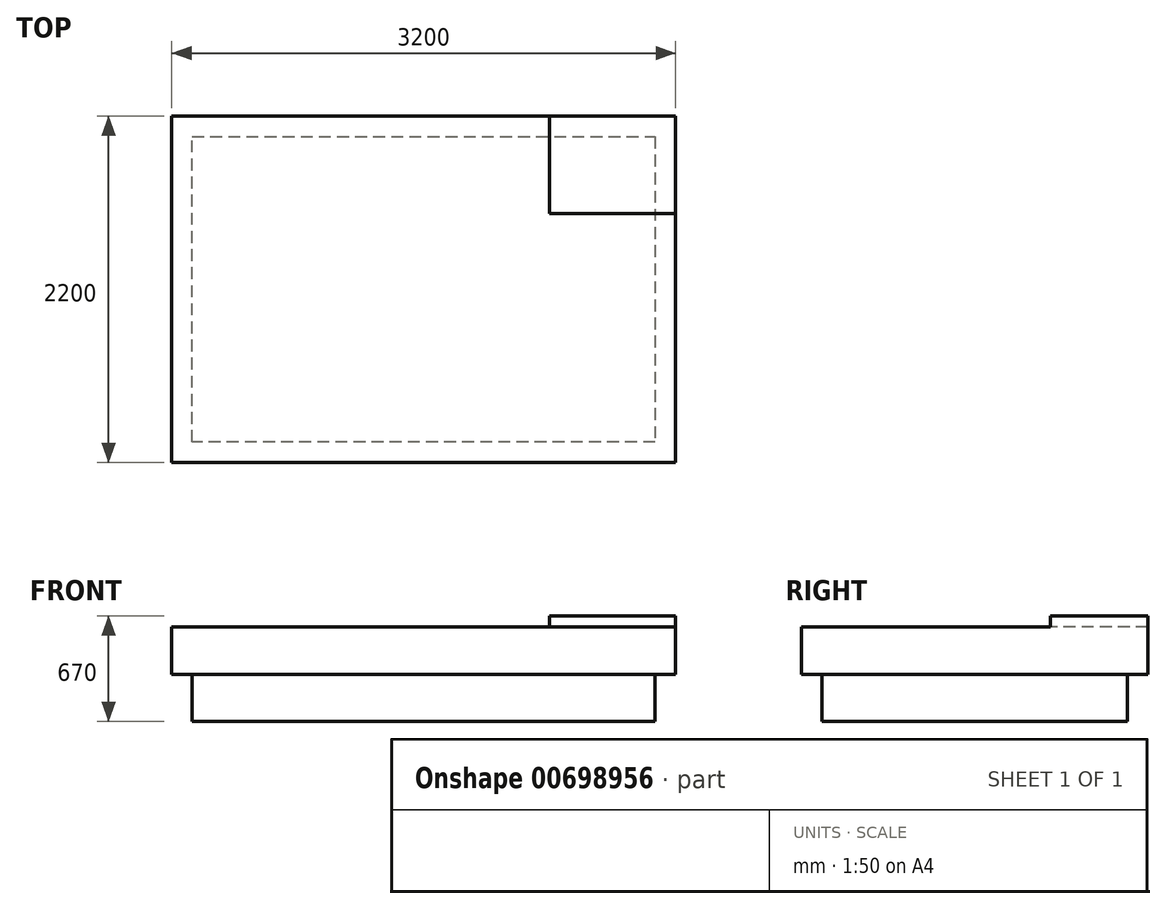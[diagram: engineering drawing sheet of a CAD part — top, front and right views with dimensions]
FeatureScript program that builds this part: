
annotation { "Feature Type Name" : "Feature", "Feature Type Description" : "" }
export const myFeature = defineFeature(function(context is Context, id is Id, definition is map)
    precondition{}
    {
        {
            var Q0;
            Q0=qCreatedBy(makeId("Top.planeOp"),FACE);
            var sketch = newSketch(context, id + "F0", { "sketchPlane" : qUnion([Q0])});
            skLineSegment(sketch, "E0.bottom", {"start": v(1600, -1100) * mm, "end": v(-1600, -1100) * mm});
            skLineSegment(sketch, "E0.top", {"start": v(1600, 1100) * mm, "end": v(-1600, 1100) * mm});
            skLineSegment(sketch, "E0.left", {"start": v(1600, -1100) * mm, "end": v(1600, 1100) * mm});
            skLineSegment(sketch, "E0.right", {"start": v(-1600, -1100) * mm, "end": v(-1600, 1100) * mm});
            skPoint(sketch, "E0.middle", {"position": v(0, 0) * mm});
            skSolve(sketch);
        }
        {
            var Q0;
            Q0 = qSketchRegion(id + "F0", true);
            extrude(context, id + "F1", {"entities" : qUnion([Q0]), "oppositeDirection" : true, "depth" : 300 * mm, "offsetDistance" : 25 * mm});
        }
        {
            var Q0;
            Q0=makeQuery(id+"F1.opExtrude","CAP_FACE",FACE,{"disambiguationData":[OSD([sQuery(id+"F0.wireOp",EDGE,"E0.bottom"),sQuery(id+"F0.wireOp",EDGE,"E0.top"),sQuery(id+"F0.wireOp",EDGE,"E0.left"),sQuery(id+"F0.wireOp",EDGE,"E0.right")])],"isStart":false});
            var sketch = newSketch(context, id + "F2", { "sketchPlane" : qUnion([Q0])});
            skLineSegment(sketch, "E1.0", {"start": v(1470, -970) * mm, "end": v(1470, 970) * mm});
            skLineSegment(sketch, "E1.1", {"start": v(-1470, -970) * mm, "end": v(1470, -970) * mm});
            skLineSegment(sketch, "E1.2", {"start": v(-1470, 970) * mm, "end": v(-1470, -970) * mm});
            skLineSegment(sketch, "E1.3", {"start": v(1470, 970) * mm, "end": v(-1470, 970) * mm});
            skSolve(sketch);
        }
        {
            var Q0;
            Q0 = qSketchRegion(id + "F2", true);
            extrude(context, id + "F3", {"entities" : qUnion([Q0]), "operationType" : NewBodyOperationType.ADD, "depth" : 300 * mm, "offsetDistance" : 25 * mm});
        }
        {
            var Q0;
            Q0=makeQuery(id+"F1.opExtrude","CAP_FACE",FACE,{"disambiguationData":[OSD([sQuery(id+"F0.wireOp",EDGE,"E0.bottom"),sQuery(id+"F0.wireOp",EDGE,"E0.top"),sQuery(id+"F0.wireOp",EDGE,"E0.left"),sQuery(id+"F0.wireOp",EDGE,"E0.right")])],"isStart":true});
            var sketch = newSketch(context, id + "F4", { "sketchPlane" : qUnion([Q0])});
            skLineSegment(sketch, "E2.bottom", {"start": v(1600, 1100) * mm, "end": v(800, 1100) * mm});
            skLineSegment(sketch, "E2.top", {"start": v(1600, 480) * mm, "end": v(800, 480) * mm});
            skLineSegment(sketch, "E2.left", {"start": v(1600, 1100) * mm, "end": v(1600, 480) * mm});
            skLineSegment(sketch, "E2.right", {"start": v(800, 1100) * mm, "end": v(800, 480) * mm});
            skSolve(sketch);
        }
        {
            var Q0;
            Q0 = qSketchRegion(id + "F4", true);
            extrude(context, id + "F5", {"entities" : qUnion([Q0]), "operationType" : NewBodyOperationType.ADD, "depth" : 70 * mm, "offsetDistance" : 25 * mm});
        }
    });
